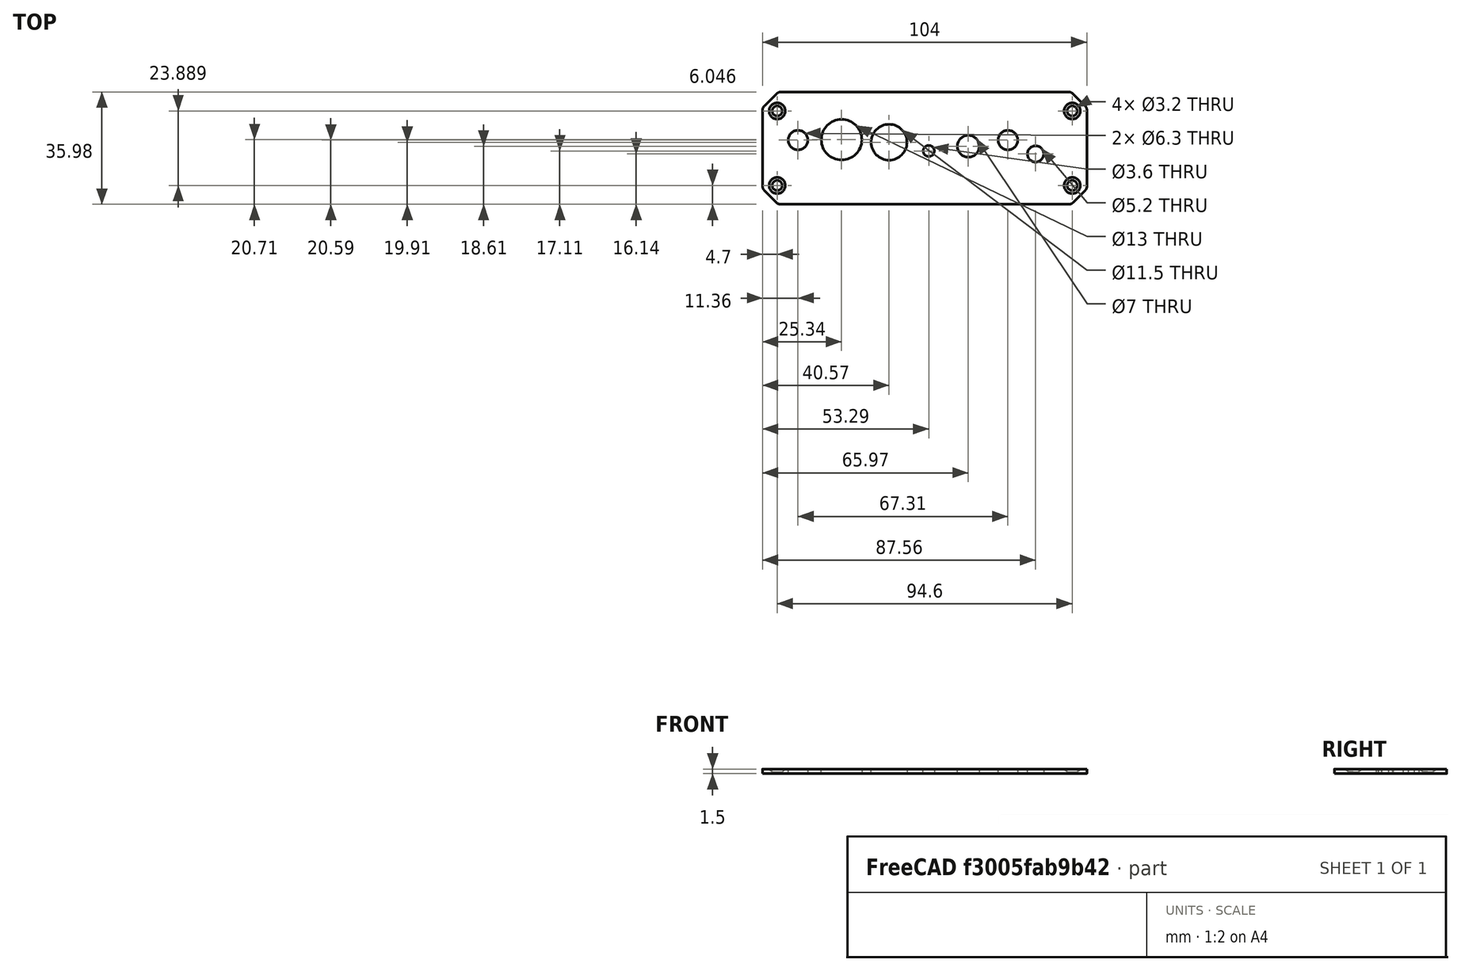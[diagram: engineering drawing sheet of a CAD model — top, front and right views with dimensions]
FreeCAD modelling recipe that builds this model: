
FCSTD DOCUMENT  (FreeCAD 1.1R14555 (Git shallow))
Label: K93-10436-H7-L120_frontpanel_generated_example
License: All rights reserved
LicenseURL: https://en.wikipedia.org/wiki/All_rights_reserved
objects: Part::Feature×1, PartDesign::FeatureBase×1, Sketcher::SketchObject×1, PartDesign::Pocket×1, PartDesign::Body×1, App::Point×1
note: 9 computed .brp shape members not serialized (recipe doc carries the construction recipe); baked Part::Feature solids carry a one-line shape summary decoded from their .brp

FEATURE [Part::Feature] Part__Feature  label="K93-B"
  shape: bbox 104 x 35.99 x 1.5 mm, 34 faces (baked)
FEATURE [PartDesign::FeatureBase] BaseFeature
  BaseFeature = -> Part__Feature
  Suppressed = false
FEATURE [Sketcher::SketchObject] Sketch
  ArcFitTolerance = 1e-06
  AttachmentSupport = -> [BaseFeature]
  ExternalTypes = [0]
  FullyConstrained = false
  MakeInternals = false
  MapMode = 5
  Placement = pos=(0,0,0.75) rot=(0,0,1;0rad)
  sketch-geometry (7):
    g0: Circle CenterX=-40.64 CenterY=2.6 CenterZ=0 NormalX=0 NormalY=0 NormalZ=1 AngleXU=0 Radius=3.15
    g1: Circle CenterX=-26.66 CenterY=2.72 CenterZ=0 NormalX=0 NormalY=0 NormalZ=1 AngleXU=0 Radius=6.5
    g2: Circle CenterX=-11.43 CenterY=1.92 CenterZ=0 NormalX=0 NormalY=0 NormalZ=1 AngleXU=0 Radius=5.75
    g3: Circle CenterX=1.29 CenterY=-0.88 CenterZ=0 NormalX=0 NormalY=0 NormalZ=1 AngleXU=0 Radius=1.8
    g4: Circle CenterX=13.97 CenterY=0.62 CenterZ=0 NormalX=0 NormalY=0 NormalZ=1 AngleXU=0 Radius=3.5
    g5: Circle CenterX=26.67 CenterY=2.6 CenterZ=0 NormalX=0 NormalY=0 NormalZ=1 AngleXU=0 Radius=3.15
    g6: Circle CenterX=35.56 CenterY=-1.85 CenterZ=0 NormalX=0 NormalY=0 NormalZ=1 AngleXU=0 Radius=2.6
FEATURE [PartDesign::Pocket] Pocket
  BaseFeature = -> BaseFeature
  Direction = (0,0,-1)
  Length = 5
  Length2 = 5
  Profile = -> Sketch
  ReferenceAxis = -> Sketch [N_Axis]
  Refine = true
  SideType = 0
  Suppressed = false
  Type = 1
  Type2 = 0
FEATURE [PartDesign::Body] Body
  AllowCompound = false
  BaseFeature = -> Part__Feature
  Group = -> [BaseFeature,Sketch,Pocket]
  Origin = -> Origin
  Tip = -> Pocket
FEATURE [App::Point] Origin001  label="Origin"
  Role = Origin
